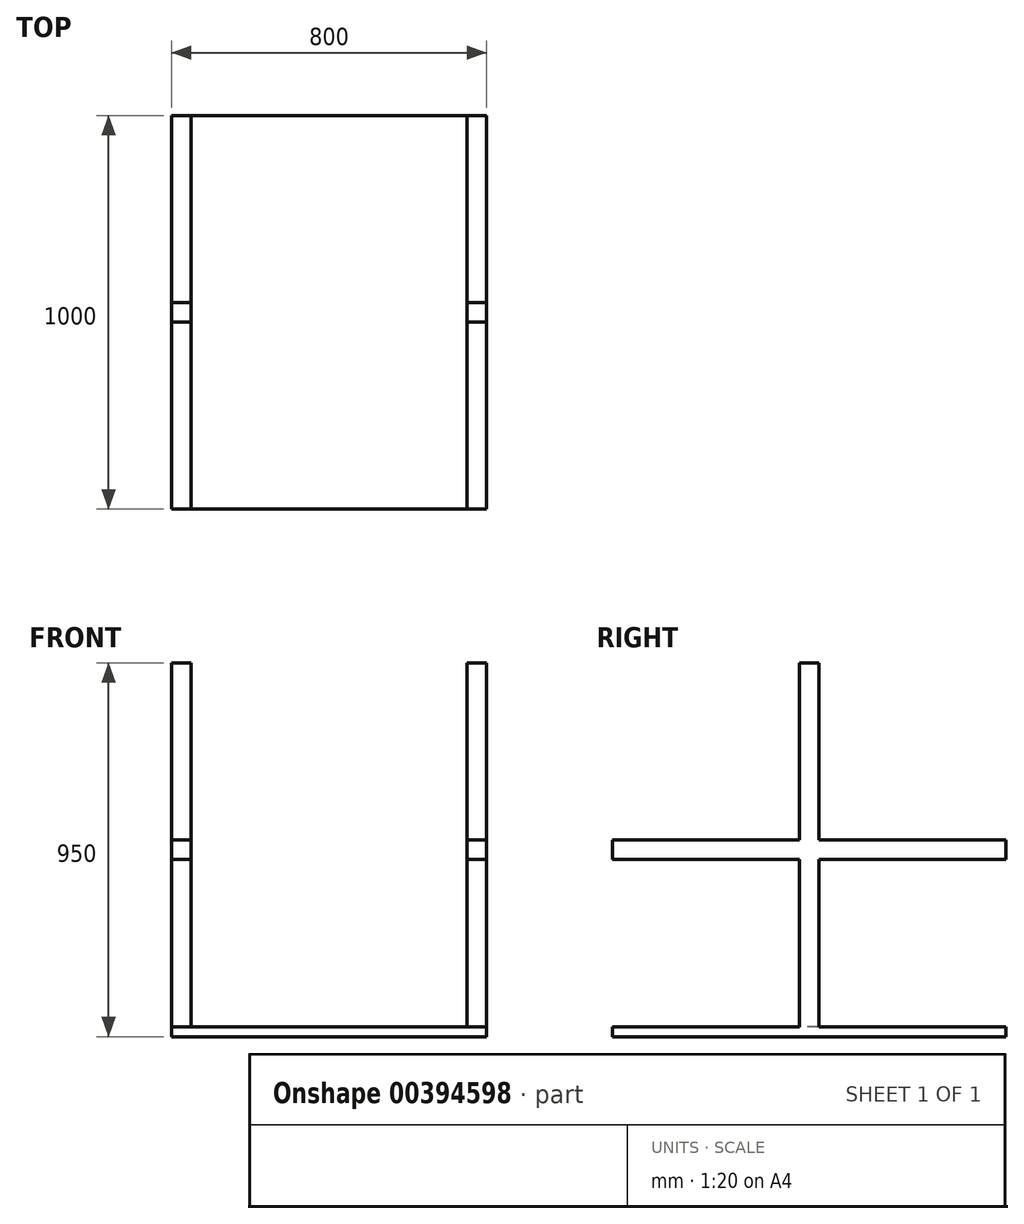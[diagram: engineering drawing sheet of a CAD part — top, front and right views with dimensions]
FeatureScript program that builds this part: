
annotation { "Feature Type Name" : "Feature", "Feature Type Description" : "" }
export const myFeature = defineFeature(function(context is Context, id is Id, definition is map)
    precondition{}
    {
        {
            var Q0;
            Q0=qCreatedBy(makeId("Top.planeOp"),FACE);
            var sketch = newSketch(context, id + "F0", { "sketchPlane" : qUnion([Q0])});
            skLineSegment(sketch, "E0.bottom", {"start": v(400, -500) * mm, "end": v(-400, -500) * mm});
            skLineSegment(sketch, "E0.top", {"start": v(400, 500) * mm, "end": v(-400, 500) * mm});
            skLineSegment(sketch, "E0.left", {"start": v(400, -500) * mm, "end": v(400, 500) * mm});
            skLineSegment(sketch, "E0.right", {"start": v(-400, -500) * mm, "end": v(-400, 500) * mm});
            skPoint(sketch, "E0.middle", {"position": v(0, 0) * mm});
            skLineSegment(sketch, "E1.bottom", {"start": v(-400, 500) * mm, "end": v(-350, 500) * mm});
            skLineSegment(sketch, "E1.top", {"start": v(-400, 450) * mm, "end": v(-350, 450) * mm});
            skLineSegment(sketch, "E1.left", {"start": v(-400, 500) * mm, "end": v(-400, 450) * mm});
            skLineSegment(sketch, "E1.right", {"start": v(-350, 500) * mm, "end": v(-350, 450) * mm});
            skLineSegment(sketch, "E2.bottom", {"start": v(400, 500) * mm, "end": v(350, 500) * mm});
            skLineSegment(sketch, "E2.top", {"start": v(400, 450) * mm, "end": v(350, 450) * mm});
            skLineSegment(sketch, "E2.left", {"start": v(400, 500) * mm, "end": v(400, 450) * mm});
            skLineSegment(sketch, "E2.right", {"start": v(350, 500) * mm, "end": v(350, 450) * mm});
            skLineSegment(sketch, "E3.bottom", {"start": v(400, -500) * mm, "end": v(350, -500) * mm});
            skLineSegment(sketch, "E3.top", {"start": v(400, -450) * mm, "end": v(350, -450) * mm});
            skLineSegment(sketch, "E3.left", {"start": v(400, -500) * mm, "end": v(400, -450) * mm});
            skLineSegment(sketch, "E3.right", {"start": v(350, -500) * mm, "end": v(350, -450) * mm});
            skLineSegment(sketch, "E4.bottom", {"start": v(-400, -500) * mm, "end": v(-350, -500) * mm});
            skLineSegment(sketch, "E4.top", {"start": v(-400, -450) * mm, "end": v(-350, -450) * mm});
            skLineSegment(sketch, "E4.left", {"start": v(-400, -500) * mm, "end": v(-400, -450) * mm});
            skLineSegment(sketch, "E4.right", {"start": v(-350, -500) * mm, "end": v(-350, -450) * mm});
            skLineSegment(sketch, "E5.bottom", {"start": v(-400, 25) * mm, "end": v(-350, 25) * mm});
            skLineSegment(sketch, "E5.top", {"start": v(-400, -25) * mm, "end": v(-350, -25) * mm});
            skLineSegment(sketch, "E5.left", {"start": v(-400, 25) * mm, "end": v(-400, -25) * mm});
            skLineSegment(sketch, "E5.right", {"start": v(-350, 25) * mm, "end": v(-350, -25) * mm});
            skLineSegment(sketch, "E6.bottom", {"start": v(400, -25) * mm, "end": v(350, -25) * mm});
            skLineSegment(sketch, "E6.top", {"start": v(400, 25) * mm, "end": v(350, 25) * mm});
            skLineSegment(sketch, "E6.left", {"start": v(400, -25) * mm, "end": v(400, 25) * mm});
            skLineSegment(sketch, "E6.right", {"start": v(350, -25) * mm, "end": v(350, 25) * mm});
            skLineSegment(sketch, "E7", {"start": v(350, 25) * mm, "end": v(350, 450) * mm});
            skLineSegment(sketch, "E8", {"start": v(350, -25) * mm, "end": v(350, -450) * mm});
            skLineSegment(sketch, "E9", {"start": v(-350, 450) * mm, "end": v(-350, 25) * mm});
            skLineSegment(sketch, "E10", {"start": v(-350, -25) * mm, "end": v(-350, -450) * mm});
            skSolve(sketch);
        }
        {
            var Q0;
            Q0=makeQuery(id+"F0.imprint","IMPRINT",FACE,{"disambiguationData":[TD([[makeQuery(id+"F0.imprint","IMPRINT",EDGE,{"derivedFrom":sQuery(id+"F0.wireOp",EDGE,"E1.bottom")}),-1.0]])]});
            var Q1;
            Q1=makeQuery(id+"F0.imprint","IMPRINT",FACE,{"disambiguationData":[TD([[makeQuery(id+"F0.imprint","IMPRINT",EDGE,{"derivedFrom":sQuery(id+"F0.wireOp",EDGE,"E5.bottom")}),-1.0]])]});
            var Q2;
            Q2=makeQuery(id+"F0.imprint","IMPRINT",FACE,{"disambiguationData":[TD([[makeQuery(id+"F0.imprint","IMPRINT",EDGE,{"derivedFrom":sQuery(id+"F0.wireOp",EDGE,"E2.bottom")}),1.0]])]});
            var Q3;
            Q3=makeQuery(id+"F0.imprint","IMPRINT",FACE,{"disambiguationData":[TD([[makeQuery(id+"F0.imprint","IMPRINT",EDGE,{"derivedFrom":sQuery(id+"F0.wireOp",EDGE,"E6.bottom")}),-1.0]])]});
            var Q4;
            Q4=makeQuery(id+"F0.imprint","IMPRINT",FACE,{"disambiguationData":[TD([[makeQuery(id+"F0.imprint","IMPRINT",EDGE,{"derivedFrom":sQuery(id+"F0.wireOp",EDGE,"E4.bottom")}),1.0]])]});
            var Q5;
            Q5=makeQuery(id+"F0.imprint","IMPRINT",FACE,{"disambiguationData":[TD([[makeQuery(id+"F0.imprint","IMPRINT",EDGE,{"derivedFrom":sQuery(id+"F0.wireOp",EDGE,"E3.bottom")}),-1.0]])]});
            extrude(context, id + "F1", {"entities" : qUnion([Q0, Q1, Q2, Q3, Q4, Q5]), "depth" : 50 * mm});
        }
        {
            var Q0;
            Q0 = qSketchRegion(id + "F0", true);
            extrude(context, id + "F2", {"entities" : qUnion([Q0]), "depth" : 25 * mm});
        }
        {
            var Q0;
            Q0=makeQuery(id+"F1.opExtrude","CAP_FACE",FACE,{"disambiguationData":[OSD([sQuery(id+"F0.wireOp",EDGE,"E4.bottom"),sQuery(id+"F0.wireOp",EDGE,"E4.top"),sQuery(id+"F0.wireOp",EDGE,"E4.left"),sQuery(id+"F0.wireOp",EDGE,"E4.right")])],"isStart":false});
            var Q1;
            Q1=makeQuery(id+"F1.opExtrude","CAP_FACE",FACE,{"disambiguationData":[OSD([sQuery(id+"F0.wireOp",EDGE,"E5.bottom"),sQuery(id+"F0.wireOp",EDGE,"E5.top"),sQuery(id+"F0.wireOp",EDGE,"E5.left"),sQuery(id+"F0.wireOp",EDGE,"E5.right")])],"isStart":false});
            var Q2;
            Q2=makeQuery(id+"F1.opExtrude","CAP_FACE",FACE,{"disambiguationData":[OSD([sQuery(id+"F0.wireOp",EDGE,"E1.bottom"),sQuery(id+"F0.wireOp",EDGE,"E1.top"),sQuery(id+"F0.wireOp",EDGE,"E1.left"),sQuery(id+"F0.wireOp",EDGE,"E1.right")])],"isStart":false});
            var Q3;
            Q3=makeQuery(id+"F1.opExtrude","CAP_FACE",FACE,{"disambiguationData":[OSD([sQuery(id+"F0.wireOp",EDGE,"E2.bottom"),sQuery(id+"F0.wireOp",EDGE,"E2.top"),sQuery(id+"F0.wireOp",EDGE,"E2.left"),sQuery(id+"F0.wireOp",EDGE,"E2.right")])],"isStart":false});
            var Q4;
            Q4=makeQuery(id+"F1.opExtrude","CAP_FACE",FACE,{"disambiguationData":[OSD([sQuery(id+"F0.wireOp",EDGE,"E6.bottom"),sQuery(id+"F0.wireOp",EDGE,"E6.top"),sQuery(id+"F0.wireOp",EDGE,"E6.left"),sQuery(id+"F0.wireOp",EDGE,"E6.right")])],"isStart":false});
            var Q5;
            Q5=makeQuery(id+"F1.opExtrude","CAP_FACE",FACE,{"disambiguationData":[OSD([sQuery(id+"F0.wireOp",EDGE,"E3.bottom"),sQuery(id+"F0.wireOp",EDGE,"E3.top"),sQuery(id+"F0.wireOp",EDGE,"E3.left"),sQuery(id+"F0.wireOp",EDGE,"E3.right")])],"isStart":false});
            extrude(context, id + "F3", {"entities" : qUnion([Q0, Q1, Q2, Q3, Q4, Q5]), "depth" : 350 * mm});
        }
        {
            var Q0;
            Q0=makeQuery(id+"F3.opExtrude","SWEPT_BODY",BODY,{"disambiguationData":[OSD([sQuery(id+"F0.wireOp",EDGE,"E1.bottom"),sQuery(id+"F0.wireOp",EDGE,"E1.top"),sQuery(id+"F0.wireOp",EDGE,"E1.left"),sQuery(id+"F0.wireOp",EDGE,"E1.right")])]});
            var Q1;
            Q1=makeQuery(id+"F3.opExtrude","SWEPT_BODY",BODY,{"disambiguationData":[OSD([sQuery(id+"F0.wireOp",EDGE,"E2.bottom"),sQuery(id+"F0.wireOp",EDGE,"E2.top"),sQuery(id+"F0.wireOp",EDGE,"E2.left"),sQuery(id+"F0.wireOp",EDGE,"E2.right")])]});
            var Q2;
            Q2=makeQuery(id+"F3.opExtrude","SWEPT_BODY",BODY,{"disambiguationData":[OSD([sQuery(id+"F0.wireOp",EDGE,"E6.bottom"),sQuery(id+"F0.wireOp",EDGE,"E6.top"),sQuery(id+"F0.wireOp",EDGE,"E6.left"),sQuery(id+"F0.wireOp",EDGE,"E6.right")])]});
            var Q3;
            Q3=makeQuery(id+"F3.opExtrude","SWEPT_BODY",BODY,{"disambiguationData":[OSD([sQuery(id+"F0.wireOp",EDGE,"E5.bottom"),sQuery(id+"F0.wireOp",EDGE,"E5.top"),sQuery(id+"F0.wireOp",EDGE,"E5.left"),sQuery(id+"F0.wireOp",EDGE,"E5.right")])]});
            var Q4;
            Q4=makeQuery(id+"F3.opExtrude","SWEPT_BODY",BODY,{"disambiguationData":[OSD([sQuery(id+"F0.wireOp",EDGE,"E4.bottom"),sQuery(id+"F0.wireOp",EDGE,"E4.top"),sQuery(id+"F0.wireOp",EDGE,"E4.left"),sQuery(id+"F0.wireOp",EDGE,"E4.right")])]});
            var Q5;
            Q5=makeQuery(id+"F3.opExtrude","SWEPT_BODY",BODY,{"disambiguationData":[OSD([sQuery(id+"F0.wireOp",EDGE,"E3.bottom"),sQuery(id+"F0.wireOp",EDGE,"E3.top"),sQuery(id+"F0.wireOp",EDGE,"E3.left"),sQuery(id+"F0.wireOp",EDGE,"E3.right")])]});
            var Q6;
            Q6=makeQuery(id+"F2.opExtrude","SWEPT_BODY",BODY,{"disambiguationData":[OSD([sQuery(id+"F0.wireOp",EDGE,"E0.bottom"),sQuery(id+"F0.wireOp",EDGE,"E0.top"),sQuery(id+"F0.wireOp",EDGE,"E0.left"),sQuery(id+"F0.wireOp",EDGE,"E0.right"),sQuery(id+"F0.wireOp",EDGE,"E1.bottom"),sQuery(id+"F0.wireOp",EDGE,"E1.left"),sQuery(id+"F0.wireOp",EDGE,"E2.bottom"),sQuery(id+"F0.wireOp",EDGE,"E2.left"),sQuery(id+"F0.wireOp",EDGE,"E3.bottom"),sQuery(id+"F0.wireOp",EDGE,"E3.left"),sQuery(id+"F0.wireOp",EDGE,"E4.bottom"),sQuery(id+"F0.wireOp",EDGE,"E4.left"),sQuery(id+"F0.wireOp",EDGE,"E5.left"),sQuery(id+"F0.wireOp",EDGE,"E6.left")])]});
            var Q7;
            Q7=makeQuery(id+"F1.opExtrude","SWEPT_BODY",BODY,{"disambiguationData":[OSD([sQuery(id+"F0.wireOp",EDGE,"E6.bottom"),sQuery(id+"F0.wireOp",EDGE,"E6.top"),sQuery(id+"F0.wireOp",EDGE,"E6.left"),sQuery(id+"F0.wireOp",EDGE,"E6.right")])]});
            var Q8;
            Q8=makeQuery(id+"F1.opExtrude","SWEPT_BODY",BODY,{"disambiguationData":[OSD([sQuery(id+"F0.wireOp",EDGE,"E4.bottom"),sQuery(id+"F0.wireOp",EDGE,"E4.top"),sQuery(id+"F0.wireOp",EDGE,"E4.left"),sQuery(id+"F0.wireOp",EDGE,"E4.right")])]});
            var Q9;
            Q9=makeQuery(id+"F1.opExtrude","SWEPT_BODY",BODY,{"disambiguationData":[OSD([sQuery(id+"F0.wireOp",EDGE,"E5.bottom"),sQuery(id+"F0.wireOp",EDGE,"E5.top"),sQuery(id+"F0.wireOp",EDGE,"E5.left"),sQuery(id+"F0.wireOp",EDGE,"E5.right")])]});
            var Q10;
            Q10=makeQuery(id+"F1.opExtrude","SWEPT_BODY",BODY,{"disambiguationData":[OSD([sQuery(id+"F0.wireOp",EDGE,"E1.bottom"),sQuery(id+"F0.wireOp",EDGE,"E1.top"),sQuery(id+"F0.wireOp",EDGE,"E1.left"),sQuery(id+"F0.wireOp",EDGE,"E1.right")])]});
            var Q11;
            Q11=makeQuery(id+"F1.opExtrude","SWEPT_BODY",BODY,{"disambiguationData":[OSD([sQuery(id+"F0.wireOp",EDGE,"E2.bottom"),sQuery(id+"F0.wireOp",EDGE,"E2.top"),sQuery(id+"F0.wireOp",EDGE,"E2.left"),sQuery(id+"F0.wireOp",EDGE,"E2.right")])]});
            var Q12;
            Q12=makeQuery(id+"F1.opExtrude","SWEPT_BODY",BODY,{"disambiguationData":[OSD([sQuery(id+"F0.wireOp",EDGE,"E3.bottom"),sQuery(id+"F0.wireOp",EDGE,"E3.top"),sQuery(id+"F0.wireOp",EDGE,"E3.left"),sQuery(id+"F0.wireOp",EDGE,"E3.right")])]});
            booleanBodies(context, id + "F4", {"operationType" : BooleanOperationType.UNION, "tools" : qUnion([Q0, Q1, Q2, Q3, Q4, Q5, Q6, Q7, Q8, Q9, Q10, Q11, Q12])});
        }
        {
            var Q0;
            Q0=makeQuery(id+"F3.opExtrude","CAP_FACE",FACE,{"disambiguationData":[OSD([sQuery(id+"F0.wireOp",EDGE,"E2.bottom"),sQuery(id+"F0.wireOp",EDGE,"E2.top"),sQuery(id+"F0.wireOp",EDGE,"E2.left"),sQuery(id+"F0.wireOp",EDGE,"E2.right")])],"isStart":false});
            var Q1;
            Q1=makeQuery(id+"F3.opExtrude","CAP_FACE",FACE,{"disambiguationData":[OSD([sQuery(id+"F0.wireOp",EDGE,"E6.bottom"),sQuery(id+"F0.wireOp",EDGE,"E6.top"),sQuery(id+"F0.wireOp",EDGE,"E6.left"),sQuery(id+"F0.wireOp",EDGE,"E6.right")])],"isStart":false});
            var Q2;
            Q2=makeQuery(id+"F3.opExtrude","CAP_FACE",FACE,{"disambiguationData":[OSD([sQuery(id+"F0.wireOp",EDGE,"E3.bottom"),sQuery(id+"F0.wireOp",EDGE,"E3.top"),sQuery(id+"F0.wireOp",EDGE,"E3.left"),sQuery(id+"F0.wireOp",EDGE,"E3.right")])],"isStart":false});
            var Q3;
            Q3=makeQuery(id+"F3.opExtrude","CAP_FACE",FACE,{"disambiguationData":[OSD([sQuery(id+"F0.wireOp",EDGE,"E4.bottom"),sQuery(id+"F0.wireOp",EDGE,"E4.top"),sQuery(id+"F0.wireOp",EDGE,"E4.left"),sQuery(id+"F0.wireOp",EDGE,"E4.right")])],"isStart":false});
            var Q4;
            Q4=makeQuery(id+"F3.opExtrude","CAP_FACE",FACE,{"disambiguationData":[OSD([sQuery(id+"F0.wireOp",EDGE,"E5.bottom"),sQuery(id+"F0.wireOp",EDGE,"E5.top"),sQuery(id+"F0.wireOp",EDGE,"E5.left"),sQuery(id+"F0.wireOp",EDGE,"E5.right")])],"isStart":false});
            var Q5;
            Q5=makeQuery(id+"F3.opExtrude","CAP_FACE",FACE,{"disambiguationData":[OSD([sQuery(id+"F0.wireOp",EDGE,"E1.bottom"),sQuery(id+"F0.wireOp",EDGE,"E1.top"),sQuery(id+"F0.wireOp",EDGE,"E1.left"),sQuery(id+"F0.wireOp",EDGE,"E1.right")])],"isStart":false});
            extrude(context, id + "F5", {"entities" : qUnion([Q0, Q1, Q2, Q3, Q4, Q5]), "operationType" : NewBodyOperationType.ADD, "depth" : 50 * mm});
        }
        {
            var Q0;
            Q0=makeQuery(id+"F5.opExtrude","CAP_FACE",FACE,{"disambiguationData":[OSD([sQuery(id+"F0.wireOp",EDGE,"E5.bottom"),sQuery(id+"F0.wireOp",EDGE,"E5.top"),sQuery(id+"F0.wireOp",EDGE,"E5.left"),sQuery(id+"F0.wireOp",EDGE,"E5.right")])],"isStart":false});
            var Q1;
            Q1=makeQuery(id+"F5.opExtrude","CAP_FACE",FACE,{"disambiguationData":[OSD([sQuery(id+"F0.wireOp",EDGE,"E6.bottom"),sQuery(id+"F0.wireOp",EDGE,"E6.top"),sQuery(id+"F0.wireOp",EDGE,"E6.left"),sQuery(id+"F0.wireOp",EDGE,"E6.right")])],"isStart":false});
            extrude(context, id + "F6", {"entities" : qUnion([Q0, Q1]), "operationType" : NewBodyOperationType.ADD, "depth" : 500 * mm});
        }
        {
            var Q0;
            {var subQ0=sQuery(id+"F0.wireOp",EDGE,"E6.left");var subQ1=sQuery(id+"F0.wireOp",EDGE,"E3.left");var subQ2=sQuery(id+"F0.wireOp",EDGE,"E2.left");Q0=makeQuery(id+"F6.boolean.opBoolean","MERGE",FACE,{"derivedFrom":[makeQuery(id+"F5.boolean.opBoolean","MERGE",FACE,{"derivedFrom":[makeQuery(id+"F4.opBoolean","MERGE",FACE,{"derivedFrom":[makeQuery(id+"F1.opExtrude","SWEPT_FACE",FACE,{"disambiguationData":[OSD([subQ2])]}),makeQuery(id+"F1.opExtrude","SWEPT_FACE",FACE,{"disambiguationData":[OSD([subQ1])]}),makeQuery(id+"F1.opExtrude","SWEPT_FACE",FACE,{"disambiguationData":[OSD([subQ0])]}),makeQuery(id+"F2.opExtrude","SWEPT_FACE",FACE,{"disambiguationData":[OSD([sQuery(id+"F0.wireOp",EDGE,"E0.left"),subQ2,subQ1,subQ0])]}),makeQuery(id+"F3.opExtrude","SWEPT_FACE",FACE,{"disambiguationData":[OSD([subQ2])]}),makeQuery(id+"F3.opExtrude","SWEPT_FACE",FACE,{"disambiguationData":[OSD([subQ1])]}),makeQuery(id+"F3.opExtrude","SWEPT_FACE",FACE,{"disambiguationData":[OSD([subQ0])]})]}),makeQuery(id+"F5.opExtrude","SWEPT_FACE",FACE,{"disambiguationData":[OSD([subQ2])]}),makeQuery(id+"F5.opExtrude","SWEPT_FACE",FACE,{"disambiguationData":[OSD([subQ1])]}),makeQuery(id+"F5.opExtrude","SWEPT_FACE",FACE,{"disambiguationData":[OSD([subQ0])]})]}),makeQuery(id+"F6.opExtrude","SWEPT_FACE",FACE,{"disambiguationData":[OSD([subQ0])]})]});}
            var sketch = newSketch(context, id + "F7", { "sketchPlane" : qUnion([Q0])});
            skLineSegment(sketch, "E11.bottom", {"start": v(-500, 450) * mm, "end": v(500, 450) * mm});
            skLineSegment(sketch, "E11.top", {"start": v(-500, 500) * mm, "end": v(500, 500) * mm});
            skLineSegment(sketch, "E11.left", {"start": v(-500, 450) * mm, "end": v(-500, 500) * mm});
            skLineSegment(sketch, "E11.right", {"start": v(500, 450) * mm, "end": v(500, 500) * mm});
            skSolve(sketch);
        }
        {
            var Q0;
            {var subQ0=sQuery(id+"F7.wireOp",EDGE,"E11.right");Q0=makeQuery(id+"F7.imprint","IMPRINT",FACE,{"disambiguationData":[TD([[makeQuery(id+"F7.imprint","IMPRINT",EDGE,{"derivedFrom":subQ0}),1.0]])]});}
            var Q1;
            {var subQ0=sQuery(id+"F7.wireOp",EDGE,"E11.left");Q1=makeQuery(id+"F7.imprint","IMPRINT",FACE,{"disambiguationData":[TD([[makeQuery(id+"F7.imprint","IMPRINT",EDGE,{"derivedFrom":subQ0}),-1.0]])]});}
            extrude(context, id + "F8", {"entities" : qUnion([Q0, Q1]), "operationType" : NewBodyOperationType.ADD, "oppositeDirection" : true, "depth" : 50 * mm});
        }
        {
            var Q0;
            {var subQ0=sQuery(id+"F0.wireOp",EDGE,"E5.left");var subQ1=sQuery(id+"F0.wireOp",EDGE,"E4.left");var subQ2=sQuery(id+"F0.wireOp",EDGE,"E1.left");Q0=makeQuery(id+"F6.boolean.opBoolean","MERGE",FACE,{"derivedFrom":[makeQuery(id+"F5.boolean.opBoolean","MERGE",FACE,{"derivedFrom":[makeQuery(id+"F4.opBoolean","MERGE",FACE,{"derivedFrom":[makeQuery(id+"F1.opExtrude","SWEPT_FACE",FACE,{"disambiguationData":[OSD([subQ2])]}),makeQuery(id+"F1.opExtrude","SWEPT_FACE",FACE,{"disambiguationData":[OSD([subQ1])]}),makeQuery(id+"F1.opExtrude","SWEPT_FACE",FACE,{"disambiguationData":[OSD([subQ0])]}),makeQuery(id+"F2.opExtrude","SWEPT_FACE",FACE,{"disambiguationData":[OSD([sQuery(id+"F0.wireOp",EDGE,"E0.right"),subQ2,subQ1,subQ0])]}),makeQuery(id+"F3.opExtrude","SWEPT_FACE",FACE,{"disambiguationData":[OSD([subQ2])]}),makeQuery(id+"F3.opExtrude","SWEPT_FACE",FACE,{"disambiguationData":[OSD([subQ1])]}),makeQuery(id+"F3.opExtrude","SWEPT_FACE",FACE,{"disambiguationData":[OSD([subQ0])]})]}),makeQuery(id+"F5.opExtrude","SWEPT_FACE",FACE,{"disambiguationData":[OSD([subQ2])]}),makeQuery(id+"F5.opExtrude","SWEPT_FACE",FACE,{"disambiguationData":[OSD([subQ1])]}),makeQuery(id+"F5.opExtrude","SWEPT_FACE",FACE,{"disambiguationData":[OSD([subQ0])]})]}),makeQuery(id+"F6.opExtrude","SWEPT_FACE",FACE,{"disambiguationData":[OSD([subQ0])]})]});}
            var sketch = newSketch(context, id + "F9", { "sketchPlane" : qUnion([Q0])});
            skLineSegment(sketch, "E12.bottom", {"start": v(-500, 450) * mm, "end": v(500, 450) * mm});
            skLineSegment(sketch, "E12.top", {"start": v(-500, 500) * mm, "end": v(500, 500) * mm});
            skLineSegment(sketch, "E12.left", {"start": v(-500, 450) * mm, "end": v(-500, 500) * mm});
            skLineSegment(sketch, "E12.right", {"start": v(500, 450) * mm, "end": v(500, 500) * mm});
            skSolve(sketch);
        }
        {
            var Q0;
            {var subQ0=sQuery(id+"F9.wireOp",EDGE,"E12.left");Q0=makeQuery(id+"F9.imprint","IMPRINT",FACE,{"disambiguationData":[TD([[makeQuery(id+"F9.imprint","IMPRINT",EDGE,{"derivedFrom":subQ0}),-1.0]])]});}
            var Q1;
            {var subQ0=sQuery(id+"F9.wireOp",EDGE,"E12.right");Q1=makeQuery(id+"F9.imprint","IMPRINT",FACE,{"disambiguationData":[TD([[makeQuery(id+"F9.imprint","IMPRINT",EDGE,{"derivedFrom":subQ0}),1.0]])]});}
            extrude(context, id + "F10", {"entities" : qUnion([Q0, Q1]), "operationType" : NewBodyOperationType.ADD, "oppositeDirection" : true, "depth" : 50 * mm});
        }
    });
